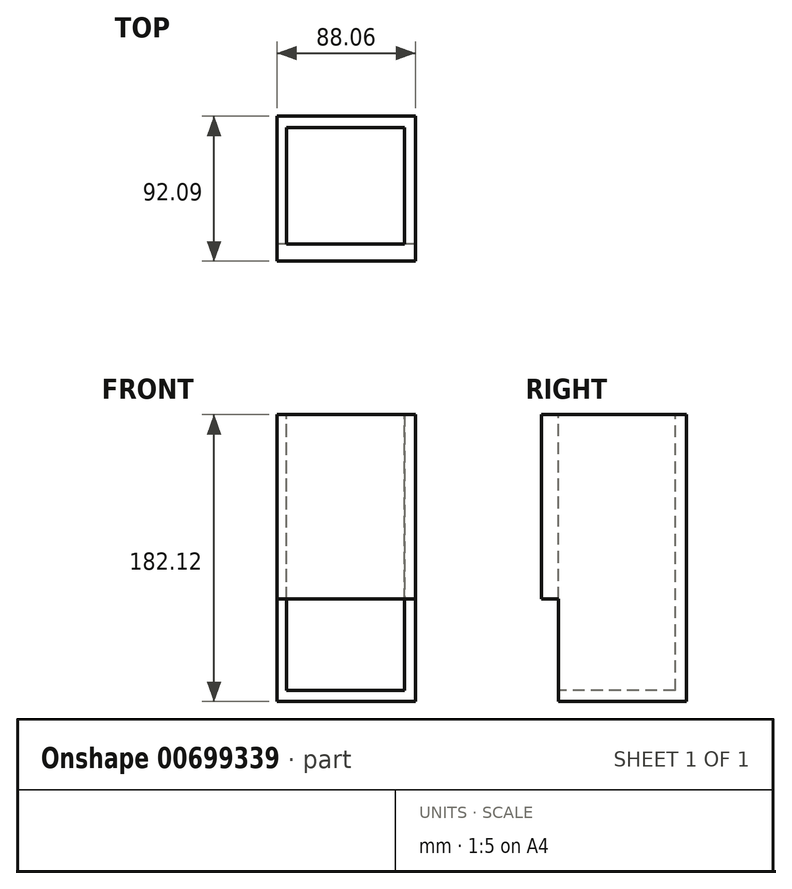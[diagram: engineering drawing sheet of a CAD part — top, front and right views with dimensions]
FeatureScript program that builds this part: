
annotation { "Feature Type Name" : "Feature", "Feature Type Description" : "" }
export const myFeature = defineFeature(function(context is Context, id is Id, definition is map)
    precondition{}
    {
        {
            var Q0;
            Q0=qCreatedBy(makeId("Top.planeOp"),FACE);
            var sketch = newSketch(context, id + "F0", { "sketchPlane" : qUnion([Q0])});
            skLineSegment(sketch, "E0.bottom", {"start": v(-42.02, 41.22) * mm, "end": v(46.04, 41.22) * mm});
            skLineSegment(sketch, "E0.top", {"start": v(-42.02, -47) * mm, "end": v(46.04, -47) * mm});
            skLineSegment(sketch, "E0.left", {"start": v(-42.02, 41.22) * mm, "end": v(-42.02, -47) * mm});
            skLineSegment(sketch, "E0.right", {"start": v(46.04, 41.22) * mm, "end": v(46.04, -47) * mm});
            skSolve(sketch);
        }
        {
            var Q0;
            Q0=makeQuery(id+"F0.imprint","IMPRINT",FACE,{"disambiguationData":[TD([[makeQuery(id+"F0.imprint","IMPRINT",EDGE,{"derivedFrom":sQuery(id+"F0.wireOp",EDGE,"E0.bottom")}),-1.0]])]});
            extrude(context, id + "F1", {"entities" : qUnion([Q0]), "depth" : 182.12 * mm, "offsetDistance" : 25.4 * mm});
        }
        {
            var Q0;
            Q0=makeQuery(id+"F1.opExtrude","CAP_FACE",FACE,{"disambiguationData":[OSD([sQuery(id+"F0.wireOp",EDGE,"E0.bottom"),sQuery(id+"F0.wireOp",EDGE,"E0.top"),sQuery(id+"F0.wireOp",EDGE,"E0.left"),sQuery(id+"F0.wireOp",EDGE,"E0.right")])],"isStart":false});
            var sketch = newSketch(context, id + "F2", { "sketchPlane" : qUnion([Q0])});
            skLineSegment(sketch, "E1.bottom", {"start": v(-36.07, 34.05) * mm, "end": v(39.07, 34.05) * mm});
            skLineSegment(sketch, "E1.top", {"start": v(-36.07, -40.1) * mm, "end": v(39.07, -40.1) * mm});
            skLineSegment(sketch, "E1.left", {"start": v(-36.07, 34.05) * mm, "end": v(-36.07, -40.1) * mm});
            skLineSegment(sketch, "E1.right", {"start": v(39.07, 34.05) * mm, "end": v(39.07, -40.1) * mm});
            skSolve(sketch);
        }
        {
            var Q0;
            Q0=makeQuery(id+"F2.imprint","IMPRINT",FACE,{"disambiguationData":[TD([[makeQuery(id+"F2.imprint","IMPRINT",EDGE,{"derivedFrom":sQuery(id+"F2.wireOp",EDGE,"E1.bottom")}),-1.0]])]});
            extrude(context, id + "F3", {"entities" : qUnion([Q0]), "operationType" : NewBodyOperationType.REMOVE, "oppositeDirection" : true, "depth" : 175.26 * mm, "offsetDistance" : 25.4 * mm});
        }
        {
            var Q0;
            Q0=makeQuery(id+"F1.opExtrude","CAP_FACE",FACE,{"disambiguationData":[OSD([sQuery(id+"F0.wireOp",EDGE,"E0.bottom"),sQuery(id+"F0.wireOp",EDGE,"E0.top"),sQuery(id+"F0.wireOp",EDGE,"E0.left"),sQuery(id+"F0.wireOp",EDGE,"E0.right")])],"isStart":false});
            var sketch = newSketch(context, id + "F4", { "sketchPlane" : qUnion([Q0])});
            skLineSegment(sketch, "E2.bottom", {"start": v(-42.02, -47) * mm, "end": v(39.07, -47) * mm});
            skLineSegment(sketch, "E2.top", {"start": v(-42.02, -40.1) * mm, "end": v(39.07, -40.1) * mm});
            skLineSegment(sketch, "E2.left", {"start": v(-42.02, -47) * mm, "end": v(-42.02, -40.1) * mm});
            skLineSegment(sketch, "E2.right", {"start": v(39.07, -47) * mm, "end": v(39.07, -40.1) * mm});
            skSolve(sketch);
        }
        {
            var Q0;
            Q0=makeQuery(id+"F4.imprint","IMPRINT",FACE,{"disambiguationData":[TD([[makeQuery(id+"F4.imprint","IMPRINT",EDGE,{"derivedFrom":sQuery(id+"F4.wireOp",EDGE,"E2.bottom")}),1.0]])]});
            extrude(context, id + "F5", {"entities" : qUnion([Q0]), "operationType" : NewBodyOperationType.REMOVE, "oppositeDirection" : true, "depth" : 183.13 * mm, "offsetDistance" : 25.4 * mm});
        }
        {
            var Q0;
            Q0=makeQuery(id+"F1.opExtrude","CAP_FACE",FACE,{"disambiguationData":[OSD([sQuery(id+"F0.wireOp",EDGE,"E0.bottom"),sQuery(id+"F0.wireOp",EDGE,"E0.top"),sQuery(id+"F0.wireOp",EDGE,"E0.left"),sQuery(id+"F0.wireOp",EDGE,"E0.right")])],"isStart":true});
            var sketch = newSketch(context, id + "F6", { "sketchPlane" : qUnion([Q0])});
            skLineSegment(sketch, "E3.bottom", {"start": v(39.07, 40.1) * mm, "end": v(46.04, 40.1) * mm});
            skLineSegment(sketch, "E3.top", {"start": v(39.07, 47) * mm, "end": v(46.04, 47) * mm});
            skLineSegment(sketch, "E3.left", {"start": v(39.07, 40.1) * mm, "end": v(39.07, 47) * mm});
            skLineSegment(sketch, "E3.right", {"start": v(46.04, 40.1) * mm, "end": v(46.04, 47) * mm});
            skSolve(sketch);
        }
        {
            var Q0;
            Q0=makeQuery(id+"F6.imprint","IMPRINT",FACE,{"disambiguationData":[TD([[makeQuery(id+"F6.imprint","IMPRINT",EDGE,{"derivedFrom":sQuery(id+"F6.wireOp",EDGE,"E3.bottom")}),1.0]])]});
            extrude(context, id + "F7", {"entities" : qUnion([Q0]), "operationType" : NewBodyOperationType.REMOVE, "oppositeDirection" : true, "depth" : 187.7 * mm, "offsetDistance" : 25.4 * mm});
        }
        {
            var Q0;
            Q0=makeQuery(id+"F1.opExtrude","CAP_FACE",FACE,{"disambiguationData":[OSD([sQuery(id+"F0.wireOp",EDGE,"E0.bottom"),sQuery(id+"F0.wireOp",EDGE,"E0.top"),sQuery(id+"F0.wireOp",EDGE,"E0.left"),sQuery(id+"F0.wireOp",EDGE,"E0.right")])],"isStart":false});
            var sketch = newSketch(context, id + "F8", { "sketchPlane" : qUnion([Q0])});
            skLineSegment(sketch, "E4.bottom", {"start": v(39.07, -40.1) * mm, "end": v(46.04, -40.1) * mm});
            skLineSegment(sketch, "E4.top", {"start": v(39.07, -50.87) * mm, "end": v(46.04, -50.87) * mm});
            skLineSegment(sketch, "E4.left", {"start": v(39.07, -40.1) * mm, "end": v(39.07, -50.87) * mm});
            skLineSegment(sketch, "E4.right", {"start": v(46.04, -40.1) * mm, "end": v(46.04, -50.87) * mm});
            skLineSegment(sketch, "E5.bottom", {"start": v(39.07, -40.1) * mm, "end": v(-42.02, -40.1) * mm});
            skLineSegment(sketch, "E5.top", {"start": v(39.07, -50.87) * mm, "end": v(-42.02, -50.87) * mm});
            skLineSegment(sketch, "E5.right", {"start": v(-42.02, -40.1) * mm, "end": v(-42.02, -50.87) * mm});
            skSolve(sketch);
        }
        {
            var Q0;
            Q0=makeQuery(id+"F8.imprint","IMPRINT",FACE,{"disambiguationData":[TD([[makeQuery(id+"F8.imprint","IMPRINT",EDGE,{"derivedFrom":sQuery(id+"F8.wireOp",EDGE,"E5.top")}),-1.0]])]});
            var Q1;
            Q1=makeQuery(id+"F8.imprint","IMPRINT",FACE,{"disambiguationData":[TD([[makeQuery(id+"F8.imprint","IMPRINT",EDGE,{"derivedFrom":sQuery(id+"F8.wireOp",EDGE,"E4.bottom")}),1.0]])]});
            extrude(context, id + "F9", {"entities" : qUnion([Q0, Q1]), "operationType" : NewBodyOperationType.ADD, "oppositeDirection" : true, "depth" : 117.1 * mm, "offsetDistance" : 25.4 * mm});
        }
    });
